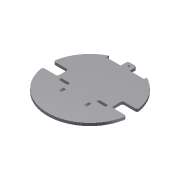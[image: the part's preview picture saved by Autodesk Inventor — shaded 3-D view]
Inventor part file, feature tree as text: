
AUTODESK INVENTOR PART (.ipt)
format: ipt  version: 2012 (Build 160160000, 160)  size: 146,432 bytes
history: native  units: mm
features: extrude x1, sketch x1
ambient origin geometry x8: Origin, YZ Plane, XZ Plane, XY Plane, X Axis, Y Axis, Z Axis, Center Point
feature tree (2):
  extrude  "Extrusion2"  Depth=10.0mm
  sketch  "Sketch1"  dims[d0=92.0mm d3=10.0mm d4=10.0mm d5=3.0mm d6=3.0mm d7=32.0mm d8=16.0mm d9=36.8mm d11=3.0mm d12=6.0mm d13=6.0mm d14=3.0mm d15=5.0mm d16=5.0mm d17=3.0mm d18=25.0mm d19=12.5mm d20=5.0mm d21=5.0mm d26=47.0mm d30=3.0mm d31=3.0mm d37=47.0mm d38=10.0mm d39=16.0mm d40=16.0mm d41=2.0mm d42=4.0mm d43=5.0mm d44=5.0mm d45=2.0mm d46=30.0mm d47=30.0mm d48=2.0mm d49=3.0mm d50=0.0mm]
